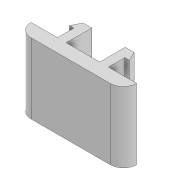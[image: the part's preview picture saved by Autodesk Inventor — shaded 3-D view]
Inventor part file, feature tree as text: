
AUTODESK INVENTOR PART (.ipt)
format: ipt  version: 2021 (Build 250183000, 183)  size: 105,472 bytes
history: native  units: mm
features: extrude x1, sketch x1
ambient origin geometry x8: Origin, YZ Plane, XZ Plane, XY Plane, X Axis, Y Axis, Z Axis, Center Point
bodies: Volumenkörper1 (feature_tree)
feature tree (2):
  extrude  "Extrusion1"  Depth=8.0mm
  sketch  "Skizze1"  dims[d0=3.0mm d1=3.0mm d2=1.0mm d3=1.0mm d4=26.947884mm d5=26.947884mm d7=0.5mm d8=3.8mm d9=2.9mm d10=9.0mm d12=5.8mm d13=0.5mm d14=2.9mm d15=4.5mm d16=0.0mm d17=8.0mm d18=0.0mm]
